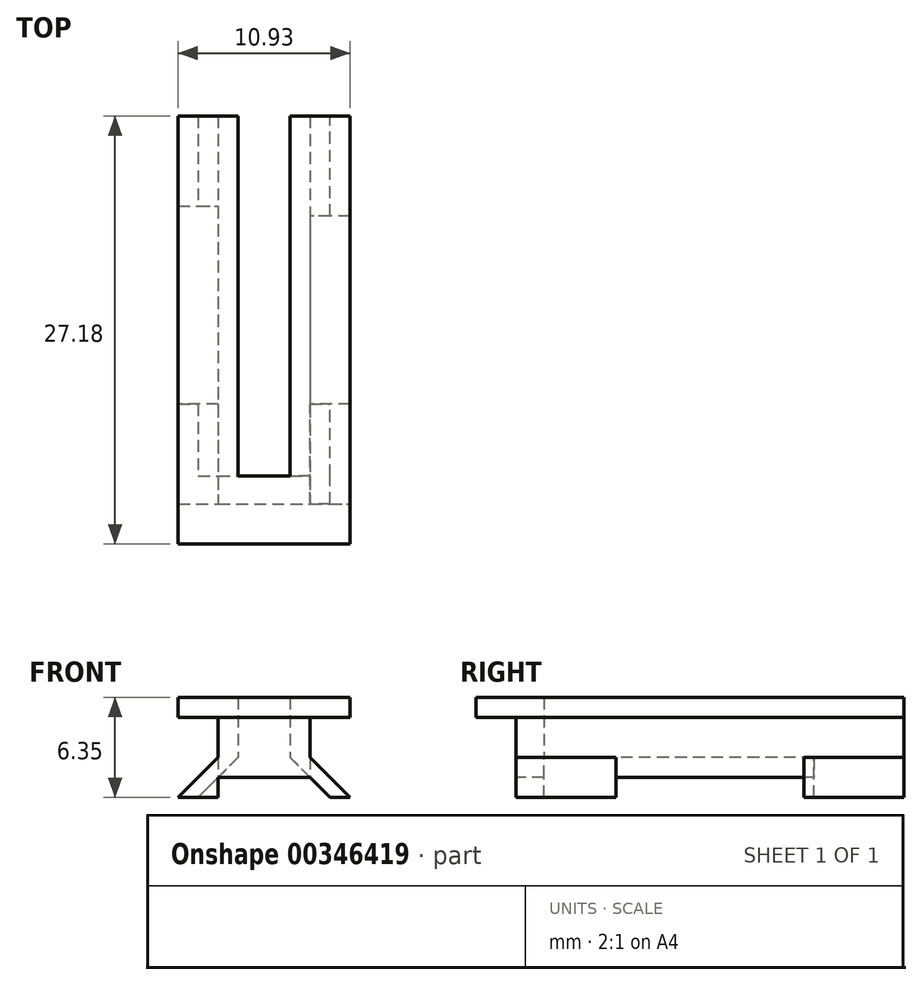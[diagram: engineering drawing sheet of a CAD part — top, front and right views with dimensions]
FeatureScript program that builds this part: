
annotation { "Feature Type Name" : "Feature", "Feature Type Description" : "" }
export const myFeature = defineFeature(function(context is Context, id is Id, definition is map)
    precondition{}
    {
        {
            var Q0;
            Q0=qCreatedBy(makeId("Top.planeOp"),FACE);
            var sketch = newSketch(context, id + "F0", { "sketchPlane" : qUnion([Q0])});
            skLineSegment(sketch, "E0.bottom", {"start": v(-56.75, 32.9) * mm, "end": v(-50.9, 32.9) * mm});
            skLineSegment(sketch, "E0.top", {"start": v(-56.75, 8.26) * mm, "end": v(-50.9, 8.26) * mm});
            skLineSegment(sketch, "E0.left", {"start": v(-56.75, 32.9) * mm, "end": v(-56.75, 8.26) * mm});
            skLineSegment(sketch, "E0.right", {"start": v(-50.9, 32.9) * mm, "end": v(-50.9, 8.26) * mm});
            skLineSegment(sketch, "E1.bottom", {"start": v(-55.48, 32.9) * mm, "end": v(-52.17, 32.9) * mm});
            skLineSegment(sketch, "E1.top", {"start": v(-55.48, 10.03) * mm, "end": v(-52.17, 10.03) * mm});
            skLineSegment(sketch, "E1.left", {"start": v(-55.48, 32.9) * mm, "end": v(-55.48, 10.03) * mm});
            skLineSegment(sketch, "E1.right", {"start": v(-52.17, 32.9) * mm, "end": v(-52.17, 10.03) * mm});
            skPoint(sketch, "E1.middle", {"position": v(-53.83, 21.47) * mm});
            skPoint(sketch, "E1.middle.positionSnap0", {"position": v(-53.83, 32.9) * mm});
            skPoint(sketch, "E1.centerSnap0", {"position": v(-53.83, 32.9) * mm});
            skSolve(sketch);
        }
        {
            var Q0;
            Q0=makeQuery(id+"F0.imprint","IMPRINT",FACE,{"disambiguationData":[TD([[makeQuery(id+"F0.imprint","IMPRINT",EDGE,{"derivedFrom":sQuery(id+"F0.wireOp",EDGE,"E0.top")}),1.0]])]});
            extrude(context, id + "F1", {"entities" : qUnion([Q0]), "depth" : 2.54 * mm, "hasSecondDirection" : true, "secondDirectionOppositeDirection" : true, "secondDirectionDepth" : 2.54 * mm, "offsetDistance" : 25.4 * mm});
        }
        {
            var Q0;
            Q0=makeQuery(id+"F1.opExtrude","CAP_FACE",FACE,{"disambiguationData":[OSD([sQuery(id+"F0.wireOp",EDGE,"E0.bottom"),sQuery(id+"F0.wireOp",EDGE,"E0.top"),sQuery(id+"F0.wireOp",EDGE,"E0.left"),sQuery(id+"F0.wireOp",EDGE,"E0.right"),sQuery(id+"F0.wireOp",EDGE,"E1.top"),sQuery(id+"F0.wireOp",EDGE,"E1.left"),sQuery(id+"F0.wireOp",EDGE,"E1.right")])],"isStart":false});
            var sketch = newSketch(context, id + "F2", { "sketchPlane" : qUnion([Q0])});
            skLineSegment(sketch, "E2.bottom", {"start": v(-55.48, 32.9) * mm, "end": v(-59.29, 32.9) * mm});
            skLineSegment(sketch, "E2.top", {"start": v(-55.48, 8.26) * mm, "end": v(-59.29, 8.26) * mm});
            skLineSegment(sketch, "E2.left", {"start": v(-55.48, 32.9) * mm, "end": v(-55.48, 8.26) * mm});
            skLineSegment(sketch, "E2.right", {"start": v(-59.29, 32.9) * mm, "end": v(-59.29, 8.26) * mm});
            skLineSegment(sketch, "E3.bottom", {"start": v(-59.29, 8.26) * mm, "end": v(-48.36, 8.26) * mm});
            skLineSegment(sketch, "E3.top", {"start": v(-59.29, 5.72) * mm, "end": v(-48.36, 5.72) * mm});
            skLineSegment(sketch, "E3.left", {"start": v(-59.29, 8.26) * mm, "end": v(-59.29, 5.72) * mm});
            skLineSegment(sketch, "E3.right", {"start": v(-48.36, 8.26) * mm, "end": v(-48.36, 5.72) * mm});
            skLineSegment(sketch, "E4.bottom", {"start": v(-48.36, 8.26) * mm, "end": v(-50.9, 8.26) * mm});
            skLineSegment(sketch, "E4.top", {"start": v(-48.36, 32.9) * mm, "end": v(-50.9, 32.9) * mm});
            skLineSegment(sketch, "E4.left", {"start": v(-48.36, 8.26) * mm, "end": v(-48.36, 32.9) * mm});
            skLineSegment(sketch, "E4.right", {"start": v(-50.9, 8.26) * mm, "end": v(-50.9, 32.9) * mm});
            skSolve(sketch);
        }
        {
            var Q0;
            Q0 = qSketchRegion(id + "F2", true);
            var Q1;
            {var subQ2=sQuery(id+"F2.wireOp",EDGE,"E4.right");Q1=makeQuery(id+"F2.imprint","IMPRINT",FACE,{"disambiguationData":[TD([[makeQuery(id+"F2.imprint","IMPRINT",EDGE,{"derivedFrom":subQ2}),-1.0]])]});}
            extrude(context, id + "F3", {"entities" : qUnion([Q0, Q1]), "operationType" : NewBodyOperationType.ADD, "depth" : 1.27 * mm});
        }
        {
            var Q0;
            Q0=makeQuery(id+"F1.opExtrude","SWEPT_FACE",FACE,{"disambiguationData":[OSD([sQuery(id+"F0.wireOp",EDGE,"E0.left")])]});
            var sketch = newSketch(context, id + "F4", { "sketchPlane" : qUnion([Q0])});
            skLineSegment(sketch, "E5", {"start": v(-32.9, 0) * mm, "end": v(-8.26, 0) * mm});
            skLineSegment(sketch, "E6", {"start": v(-27.19, 0) * mm, "end": v(-27.19, -2.54) * mm});
            skLineSegment(sketch, "E7", {"start": v(-14.61, 0) * mm, "end": v(-14.61, -2.54) * mm});
            skSolve(sketch);
        }
        {
            var Q0;
            Q0=makeQuery(id+"F1.opExtrude","SWEPT_FACE",FACE,{"disambiguationData":[OSD([sQuery(id+"F0.wireOp",EDGE,"E0.right")])]});
            var sketch = newSketch(context, id + "F5", { "sketchPlane" : qUnion([Q0])});
            skLineSegment(sketch, "E8", {"start": v(32.9, 0) * mm, "end": v(26.55, 0) * mm});
            skLineSegment(sketch, "E9", {"start": v(26.55, 0) * mm, "end": v(26.55, -2.54) * mm});
            skLineSegment(sketch, "E10", {"start": v(8.26, 0) * mm, "end": v(14.61, 0) * mm});
            skPoint(sketch, "E10.endSnap0", {"position": v(8.26, 0) * mm});
            skLineSegment(sketch, "E11", {"start": v(14.61, 0) * mm, "end": v(14.61, -2.54) * mm});
            skSolve(sketch);
        }
        {
            var Q0;
            {var subQ4=sQuery(id+"F4.wireOp",EDGE,"E6");Q0=makeQuery(id+"F4.imprint","IMPRINT",FACE,{"disambiguationData":[TD([[makeQuery(id+"F4.imprint","IMPRINT",EDGE,{"derivedFrom":subQ4}),-1.0]])]});}
            var Q1;
            {var subQ4=sQuery(id+"F4.wireOp",EDGE,"E7");Q1=makeQuery(id+"F4.imprint","IMPRINT",FACE,{"disambiguationData":[TD([[makeQuery(id+"F4.imprint","IMPRINT",EDGE,{"derivedFrom":subQ4}),1.0]])]});}
            extrude(context, id + "F6", {"entities" : qUnion([Q0, Q1]), "operationType" : NewBodyOperationType.ADD, "depth" : 2.54 * mm, "offsetDistance" : 25.4 * mm});
        }
        {
            var Q0;
            {var subQ0=sQuery(id+"F5.wireOp",EDGE,"E8");Q0=makeQuery(id+"F5.imprint","IMPRINT",FACE,{"disambiguationData":[TD([[makeQuery(id+"F5.imprint","IMPRINT",EDGE,{"derivedFrom":subQ0}),1.0]])]});}
            var Q1;
            {var subQ0=sQuery(id+"F5.wireOp",EDGE,"E10");Q1=makeQuery(id+"F5.imprint","IMPRINT",FACE,{"disambiguationData":[TD([[makeQuery(id+"F5.imprint","IMPRINT",EDGE,{"derivedFrom":subQ0}),-1.0]])]});}
            extrude(context, id + "F7", {"entities" : qUnion([Q0, Q1]), "operationType" : NewBodyOperationType.ADD, "depth" : 2.54 * mm, "offsetDistance" : 25.4 * mm});
        }
        {
            var Q0;
            Q0=makeQuery(id+"F7.opExtrude","CAP_EDGE",EDGE,{"disambiguationData":[OSD([sQuery(id+"F5.wireOp",EDGE,"E8")])],"isStart":false});
            var Q1;
            Q1=makeQuery(id+"F7.opExtrude","CAP_EDGE",EDGE,{"disambiguationData":[OSD([sQuery(id+"F5.wireOp",EDGE,"E10")])],"isStart":false});
            var Q2;
            Q2=makeQuery(id+"F1.opExtrude","CAP_EDGE",EDGE,{"disambiguationData":[OSD([sQuery(id+"F0.wireOp",EDGE,"E1.right")])],"isStart":true});
            var Q3;
            Q3=makeQuery(id+"F6.opExtrude","CAP_EDGE",EDGE,{"disambiguationData":[OSD([sQuery(id+"F4.wireOp",EDGE,"E5")])],"isStart":false});
            var Q4;
            Q4=makeQuery(id+"F1.opExtrude","CAP_EDGE",EDGE,{"disambiguationData":[OSD([sQuery(id+"F0.wireOp",EDGE,"E1.left")])],"isStart":true});
            chamfer(context, id + "F8", {"entities" : qUnion([Q0, Q1, Q2, Q3, Q4]), "width" : 2.54 * mm, "tangentPropagation" : true});
        }
        {
            var Q0;
            {var subQ0=sQuery(id+"F0.wireOp",EDGE,"E0.right");var subQ1=makeQuery(id+"F1.opExtrude","CAP_EDGE",EDGE,{"disambiguationData":[OSD([subQ0])],"isStart":true});var subQ2=sQuery(id+"F0.wireOp",EDGE,"E0.top");var subQ3=sQuery(id+"F0.wireOp",EDGE,"E0.bottom");var subQ4=sQuery(id+"F0.wireOp",EDGE,"E0.left");var subQ5=makeQuery(id+"F1.opExtrude","CAP_EDGE",EDGE,{"disambiguationData":[OSD([subQ4])],"isStart":true});Q0=makeQuery(id+"F8.opChamfer","SPLIT",FACE,{"disambiguationData":[OD(2.0)],"derivedFrom":makeQuery(id+"F7.boolean.opBoolean","MERGE",FACE,{"derivedFrom":[makeQuery(id+"F6.boolean.opBoolean","MERGE",FACE,{"derivedFrom":[makeQuery(id+"F1.opExtrude","CAP_FACE",FACE,{"disambiguationData":[OSD([subQ3,subQ2,subQ4,subQ0,sQuery(id+"F0.wireOp",EDGE,"E1.top"),sQuery(id+"F0.wireOp",EDGE,"E1.left"),sQuery(id+"F0.wireOp",EDGE,"E1.right")])],"isStart":true}),makeQuery(id+"F6.opExtrude","SWEPT_FACE",FACE,{"disambiguationData":[OSD([subQ4]),TDD([makeQuery(id+"F4.imprint","IMPRINT",EDGE,{"disambiguationData":[TD([[makeQuery(id+"F4.imprint","INTERSECT",VERTEX,{"derivedFrom":[subQ5,sQuery(id+"F4.wireOp",EDGE,"E6")]}),1.0]])],"derivedFrom":subQ5})])]}),makeQuery(id+"F6.opExtrude","SWEPT_FACE",FACE,{"disambiguationData":[OSD([subQ4]),TDD([makeQuery(id+"F4.imprint","IMPRINT",EDGE,{"disambiguationData":[TD([[makeQuery(id+"F4.imprint","INTERSECT",VERTEX,{"derivedFrom":[subQ5,sQuery(id+"F4.wireOp",EDGE,"E7")]}),-1.0]])],"derivedFrom":subQ5})])]})]}),makeQuery(id+"F7.opExtrude","SWEPT_FACE",FACE,{"disambiguationData":[OSD([subQ0]),TDD([makeQuery(id+"F5.imprint","IMPRINT",EDGE,{"disambiguationData":[TD([[makeQuery(id+"F5.imprint","INTERSECT",VERTEX,{"derivedFrom":[subQ1,sQuery(id+"F5.wireOp",EDGE,"E9")]}),1.0]])],"derivedFrom":subQ1})])]}),makeQuery(id+"F7.opExtrude","SWEPT_FACE",FACE,{"disambiguationData":[OSD([subQ0]),TDD([makeQuery(id+"F5.imprint","IMPRINT",EDGE,{"disambiguationData":[TD([[makeQuery(id+"F5.imprint","INTERSECT",VERTEX,{"derivedFrom":[subQ1,sQuery(id+"F5.wireOp",EDGE,"E11")]}),-1.0]])],"derivedFrom":subQ1})])]})]})});}
            var sketch = newSketch(context, id + "F9", { "sketchPlane" : qUnion([Q0])});
            skLineSegment(sketch, "E12", {"start": v(-49.63, -10.03) * mm, "end": v(-49.63, -8.26) * mm});
            skLineSegment(sketch, "E13", {"start": v(-58.02, -10.03) * mm, "end": v(-58.02, -8.26) * mm});
            skLineSegment(sketch, "E14", {"start": v(-50.9, -10.03) * mm, "end": v(-50.9, -8.26) * mm});
            skLineSegment(sketch, "E15", {"start": v(-56.75, -10.03) * mm, "end": v(-56.75, -8.26) * mm});
            skSolve(sketch);
        }
        {
            var Q0;
            {var subQ0=sQuery(id+"F9.wireOp",EDGE,"E14");Q0=makeQuery(id+"F9.imprint","IMPRINT",FACE,{"disambiguationData":[TD([[makeQuery(id+"F9.imprint","IMPRINT",EDGE,{"derivedFrom":subQ0}),1.0]])]});}
            extrude(context, id + "F10", {"entities" : qUnion([Q0]), "operationType" : NewBodyOperationType.REMOVE, "oppositeDirection" : true, "depth" : 1.27 * mm, "offsetDistance" : 25.4 * mm});
        }
        {
            var Q0;
            Q0=makeQuery(id+"F10.boolean.opBoolean","COPY",EDGE,{"derivedFrom":makeQuery(id+"F10.opExtrude","CAP_EDGE",EDGE,{"disambiguationData":[OSD([sQuery(id+"F9.wireOp",EDGE,"E14")])],"isStart":true})});
            var Q1;
            Q1=makeQuery(id+"F10.boolean.opBoolean","COPY",EDGE,{"derivedFrom":makeQuery(id+"F10.opExtrude","CAP_EDGE",EDGE,{"disambiguationData":[OSD([sQuery(id+"F9.wireOp",EDGE,"E15")])],"isStart":true})});
            chamfer(context, id + "F11", {"entities" : qUnion([Q0, Q1]), "width" : 1.27 * mm, "tangentPropagation" : true});
        }
    });
